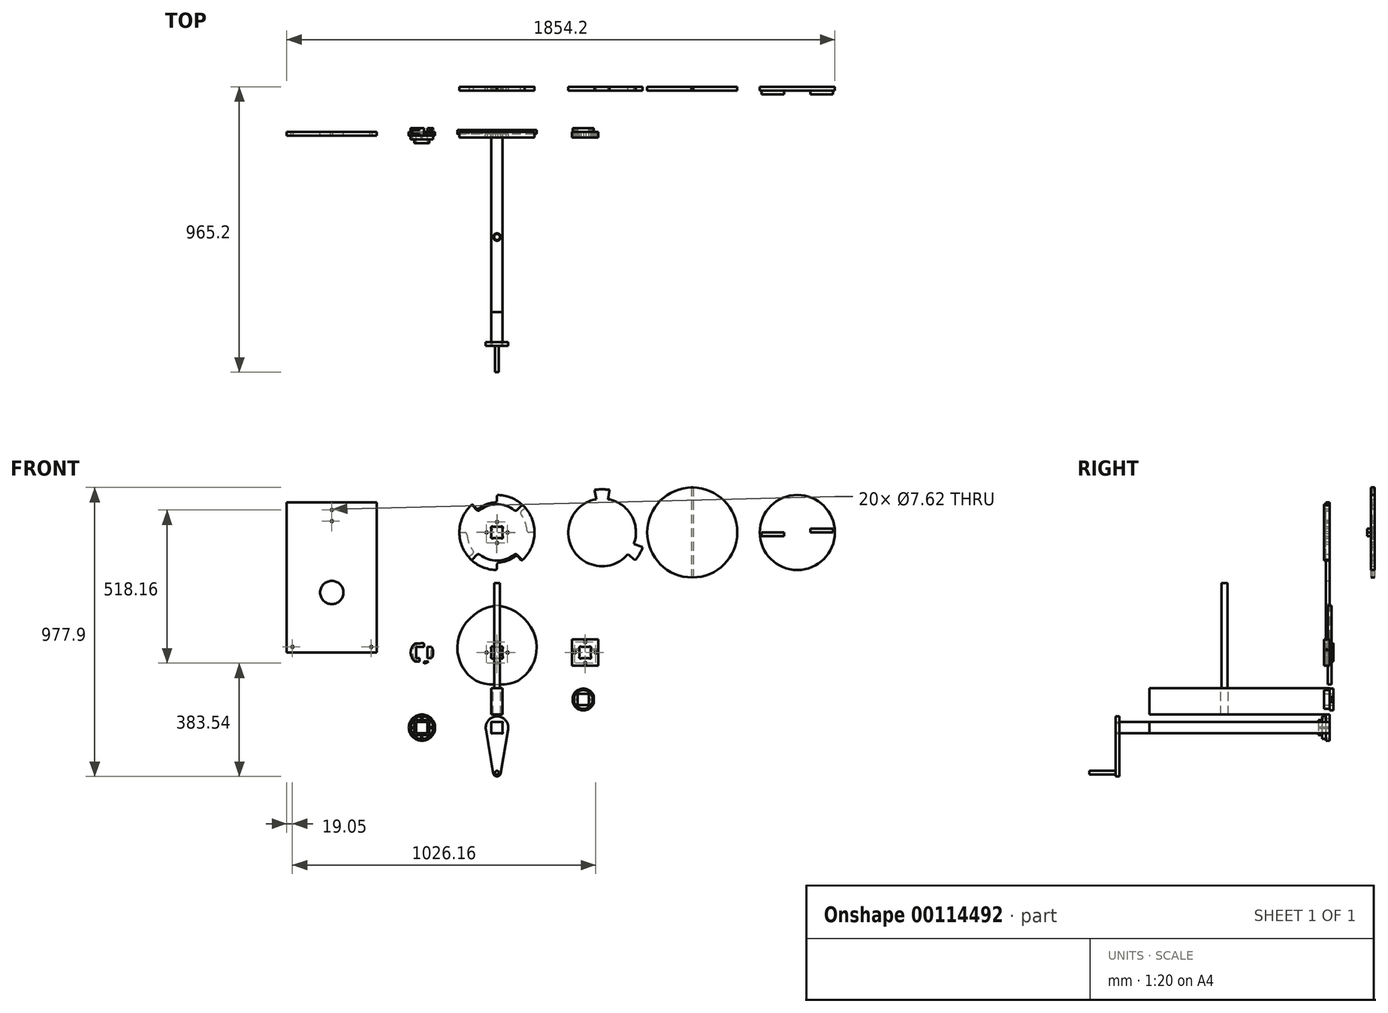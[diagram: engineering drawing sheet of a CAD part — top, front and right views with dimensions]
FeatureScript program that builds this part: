
annotation { "Feature Type Name" : "Feature", "Feature Type Description" : "" }
export const myFeature = defineFeature(function(context is Context, id is Id, definition is map)
    precondition{}
    {
        {
            var Q0;
            Q0=qCreatedBy(makeId("Front.planeOp"),FACE);
            var sketch = newSketch(context, id + "F0", { "sketchPlane" : qUnion([Q0])});
            skLineSegment(sketch, "E0", {"start": v(-177.8, 0) * mm, "end": v(177.8, 0) * mm, "construction": true});
            skLineSegment(sketch, "E1", {"start": v(0, 177.8) * mm, "end": v(0, -177.8) * mm, "construction": true});
            skLineSegment(sketch, "E2.bottom", {"start": v(-12.7, -19.05) * mm, "end": v(12.7, -19.05) * mm});
            skLineSegment(sketch, "E2.top", {"start": v(-12.7, 19.05) * mm, "end": v(12.7, 19.05) * mm});
            skLineSegment(sketch, "E2.left", {"start": v(-19.05, -12.7) * mm, "end": v(-19.05, 12.7) * mm});
            skLineSegment(sketch, "E2.right", {"start": v(19.05, -12.7) * mm, "end": v(19.05, 12.7) * mm});
            skCircle(sketch, "E3", {"center": v(0, 0) * mm, "radius": 107.95 * mm, "construction": true});
            skCircle(sketch, "E4", {"center": v(0, 0) * mm, "radius": 158.75 * mm, "construction": true});
            skLineSegment(sketch, "E5", {"start": v(0, 0) * mm, "end": v(92.23, -159.75) * mm, "construction": true});
            skLineSegment(sketch, "E6", {"start": v(0, 0) * mm, "end": v(167.52, -96.72) * mm, "construction": true});
            skLineSegment(sketch, "E7", {"start": v(0, 0) * mm, "end": v(165.07, 95.3) * mm, "construction": true});
            skLineSegment(sketch, "E8", {"start": v(0, 0) * mm, "end": v(94.16, 163.09) * mm, "construction": true});
            skLineSegment(sketch, "E9", {"start": v(0, 0) * mm, "end": v(-88.3, 152.95) * mm, "construction": true});
            skLineSegment(sketch, "E10", {"start": v(0, 0) * mm, "end": v(-155.29, 89.66) * mm, "construction": true});
            skLineSegment(sketch, "E11", {"start": v(0, 0) * mm, "end": v(-153.33, -88.52) * mm, "construction": true});
            skLineSegment(sketch, "E12", {"start": v(0, 0) * mm, "end": v(-90.3, -156.42) * mm, "construction": true});
            skPoint(sketch, "E13", {"position": v(0, -107.95) * mm});
            skPoint(sketch, "E14", {"position": v(58.17, -100.75) * mm});
            skPoint(sketch, "E15", {"position": v(108, -62.36) * mm});
            skPoint(sketch, "E16", {"position": v(133.1, 0) * mm});
            skPoint(sketch, "E17", {"position": v(122.52, 70.74) * mm});
            skPoint(sketch, "E18", {"position": v(74.93, 129.78) * mm});
            skPoint(sketch, "E19", {"position": v(0, 158.75) * mm});
            skPoint(sketch, "E20.MirrorP", {"position": v(-74.93, 129.78) * mm});
            skPoint(sketch, "E21.MirrorP", {"position": v(-133.1, 0) * mm});
            skPoint(sketch, "E22.MirrorP", {"position": v(-108, -62.36) * mm});
            skPoint(sketch, "E23.MirrorP", {"position": v(-58.17, -100.75) * mm});
            skPoint(sketch, "E24.MirrorP", {"position": v(-122.52, 70.74) * mm});
            skFitSpline(sketch, "E25", {"points": [v(0, 158.75) * mm, v(-74.93, 129.78) * mm, v(-122.52, 70.74) * mm, v(-133.1, 0) * mm, v(-108, -62.36) * mm, v(-58.17, -100.75) * mm, v(0, -107.95) * mm, v(58.17, -100.75) * mm, v(108, -62.36) * mm, v(133.1, 0) * mm, v(122.52, 70.74) * mm, v(74.93, 129.78) * mm, v(0, 158.75) * mm]});
            skPoint(sketch, "E26.visualSharp", {"position": v(-19.05, 19.05) * mm});
            skPoint(sketch, "E27.visualSharp", {"position": v(19.05, 19.05) * mm});
            skPoint(sketch, "E28.visualSharp", {"position": v(19.05, -19.05) * mm});
            skPoint(sketch, "E29.visualSharp", {"position": v(-19.05, -19.05) * mm});
            skArc(sketch, "E30", {"start": v(-12.7, 19.05) * mm, "mid": v(-19.05, 19.05) * mm, "end": v(-19.05, 12.7) * mm});
            skLineSegment(sketch, "E31", {"start": v(-19.05, 12.7) * mm, "end": v(-19.05, 19.05) * mm, "construction": true});
            skLineSegment(sketch, "E32", {"start": v(-12.7, 19.05) * mm, "end": v(-19.05, 19.05) * mm, "construction": true});
            skLineSegment(sketch, "E33", {"start": v(-19.05, -12.7) * mm, "end": v(-19.05, -19.05) * mm, "construction": true});
            skLineSegment(sketch, "E34", {"start": v(-12.7, -19.05) * mm, "end": v(-19.05, -19.05) * mm, "construction": true});
            skArc(sketch, "E35", {"start": v(-19.05, -12.7) * mm, "mid": v(-19.05, -19.05) * mm, "end": v(-12.7, -19.05) * mm});
            skArc(sketch, "E36.MirrorC", {"start": v(12.7, 19.05) * mm, "mid": v(19.05, 19.05) * mm, "end": v(19.05, 12.7) * mm});
            skArc(sketch, "E37.MirrorC", {"start": v(19.05, -12.7) * mm, "mid": v(19.05, -19.05) * mm, "end": v(12.7, -19.05) * mm});
            skCircle(sketch, "E38", {"center": v(0, 35.56) * mm, "radius": 3.81 * mm});
            skCircle(sketch, "E39.MirrorC", {"center": v(0, -35.56) * mm, "radius": 3.81 * mm});
            skCircle(sketch, "E40", {"center": v(-35.56, 0) * mm, "radius": 3.81 * mm});
            skCircle(sketch, "E41.MirrorC", {"center": v(35.56, 0) * mm, "radius": 3.81 * mm});
            skSolve(sketch);
        }
        {
            var Q0;
            Q0=makeQuery(id+"F0.imprint","IMPRINT",FACE,{"disambiguationData":[TD([[makeQuery(id+"F0.imprint","IMPRINT",EDGE,{"derivedFrom":sQuery(id+"F0.wireOp",EDGE,"E2.bottom")}),-1.0]])]});
            extrude(context, id + "F1", {"entities" : qUnion([Q0]), "endBound" : BoundingType.SYMMETRIC, "depth" : 12.7 * mm});
        }
        {
            var Q0;
            Q0=qCreatedBy(makeId("Right.planeOp"),FACE);
            cPlane(context, id + "F2", {"entities" : qUnion([Q0]), "cplaneType" : CPlaneType.OFFSET, "offset" : 254 * mm, "oppositeDirection" : true, "width" : 152.4 * mm, "height" : 152.4 * mm});
        }
        {
            var Q0;
            Q0=qCreatedBy(makeId("Front.planeOp"),FACE);
            var sketch = newSketch(context, id + "F3", { "sketchPlane" : qUnion([Q0])});
            skPoint(sketch, "E42", {"position": v(-254, 0) * mm});
            skCircle(sketch, "E43", {"center": v(-254, 0) * mm, "radius": 38.1 * mm});
            skCircle(sketch, "E44", {"center": v(-254, 0) * mm, "radius": 31.75 * mm});
            skLineSegment(sketch, "E45", {"start": v(-254, -101.35) * mm, "end": v(-254, 100.54) * mm, "construction": true});
            skLineSegment(sketch, "E46", {"start": v(-330.2, 0) * mm, "end": v(-154.12, 0) * mm, "construction": true});
            skLineSegment(sketch, "E47.bottom", {"start": v(-273.05, -19.05) * mm, "end": v(-234.95, -19.05) * mm});
            skLineSegment(sketch, "E47.top", {"start": v(-273.05, 19.05) * mm, "end": v(-234.95, 19.05) * mm});
            skLineSegment(sketch, "E47.left", {"start": v(-273.05, -19.05) * mm, "end": v(-273.05, 19.05) * mm});
            skLineSegment(sketch, "E47.right", {"start": v(-234.95, -19.05) * mm, "end": v(-234.95, 19.05) * mm});
            skLineSegment(sketch, "E48", {"start": v(-246.38, 37.33) * mm, "end": v(-246.38, -37.33) * mm});
            skLineSegment(sketch, "E49.MirrorCS", {"start": v(-261.62, 37.33) * mm, "end": v(-261.62, -37.33) * mm});
            skLineSegment(sketch, "E50", {"start": v(-231.6, 30.82) * mm, "end": v(-276.4, 30.82) * mm});
            skLineSegment(sketch, "E51.MirrorCS", {"start": v(-231.6, -30.82) * mm, "end": v(-276.4, -30.82) * mm});
            skPoint(sketch, "E52", {"position": v(-261.62, 30.82) * mm});
            skLineSegment(sketch, "E53", {"start": v(-234.95, 19.05) * mm, "end": v(-221, 19.05) * mm});
            skLineSegment(sketch, "E54", {"start": v(-234.95, -19.05) * mm, "end": v(-221, -19.05) * mm});
            skSolve(sketch);
        }
        {
            var Q0;
            {var subQ0=sQuery(id+"F3.wireOp",EDGE,"E47.left");Q0=makeQuery(id+"F3.imprint","IMPRINT",FACE,{"disambiguationData":[TD([[makeQuery(id+"F3.imprint","IMPRINT",EDGE,{"derivedFrom":subQ0}),1.0]])]});}
            extrude(context, id + "F4", {"entities" : qUnion([Q0]), "depth" : 6.35 * mm});
        }
        {
            var Q0;
            {var subQ6=sQuery(id+"F3.wireOp",EDGE,"E50");var subQ8=sQuery(id+"F3.wireOp",EDGE,"E43");var subQ9=makeQuery(id+"F3.imprint","INTERSECT",VERTEX,{"disambiguationData":[OD(1.0)],"derivedFrom":[subQ8,subQ6]});Q0=makeQuery(id+"F3.imprint","IMPRINT",FACE,{"disambiguationData":[TD([[makeQuery(id+"F3.imprint","IMPRINT",EDGE,{"disambiguationData":[TD([[subQ9,-1.0]])],"derivedFrom":subQ8}),1.0]])]});}
            var Q1;
            {var subQ0=sQuery(id+"F3.wireOp",EDGE,"E47.left");Q1=makeQuery(id+"F3.imprint","IMPRINT",FACE,{"disambiguationData":[TD([[makeQuery(id+"F3.imprint","IMPRINT",EDGE,{"derivedFrom":subQ0}),1.0]])]});}
            extrude(context, id + "F5", {"entities" : qUnion([Q0, Q1]), "operationType" : NewBodyOperationType.ADD, "depth" : 12.7 * mm, "hasSecondDirection" : true, "secondDirectionOppositeDirection" : false, "secondDirectionDepth" : 6.35 * mm});
        }
        {
            var Q0;
            Q0=makeQuery(id+"F4.opExtrude","SWEPT_BODY",BODY,{"disambiguationData":[OSD([sQuery(id+"F3.wireOp",EDGE,"E44"),sQuery(id+"F3.wireOp",EDGE,"E47.bottom"),sQuery(id+"F3.wireOp",EDGE,"E47.top"),sQuery(id+"F3.wireOp",EDGE,"E47.left"),sQuery(id+"F3.wireOp",EDGE,"E49.MirrorCS")])]});
            var Q1;
            Q1=qCreatedBy(makeId("Front.planeOp"),FACE);
            mirror(context, id + "F6", {"operationType" : NewBodyOperationType.ADD, "entities" : qUnion([Q0]), "mirrorPlane" : qUnion([Q1])});
        }
        {
            var Q0;
            Q0=qCreatedBy(makeId("Front.planeOp"),FACE);
            var sketch = newSketch(context, id + "F7", { "sketchPlane" : qUnion([Q0])});
            skLineSegment(sketch, "E55.bottom", {"start": v(-406.4, 0) * mm, "end": v(-711.2, 0) * mm});
            skLineSegment(sketch, "E55.top", {"start": v(-406.4, 508) * mm, "end": v(-711.2, 508) * mm});
            skLineSegment(sketch, "E55.left", {"start": v(-406.4, 0) * mm, "end": v(-406.4, 508) * mm});
            skLineSegment(sketch, "E55.right", {"start": v(-711.2, 0) * mm, "end": v(-711.2, 508) * mm});
            skLineSegment(sketch, "E56", {"start": v(-558.8, 508) * mm, "end": v(-558.8, 0) * mm, "construction": true});
            skLineSegment(sketch, "E57", {"start": v(-711.2, 254) * mm, "end": v(-406.4, 254) * mm, "construction": true});
            skCircle(sketch, "E58", {"center": v(-558.8, 203.2) * mm, "radius": 39.37 * mm});
            skLineSegment(sketch, "E59.bottom", {"start": v(-577.85, 508) * mm, "end": v(-539.75, 508) * mm, "construction": true});
            skLineSegment(sketch, "E59.top", {"start": v(-577.85, 419.1) * mm, "end": v(-539.75, 419.1) * mm, "construction": true});
            skLineSegment(sketch, "E59.left", {"start": v(-577.85, 508) * mm, "end": v(-577.85, 419.1) * mm, "construction": true});
            skLineSegment(sketch, "E59.right", {"start": v(-539.75, 508) * mm, "end": v(-539.75, 419.1) * mm, "construction": true});
            skCircle(sketch, "E60", {"center": v(-558.8, 482.6) * mm, "radius": 3.81 * mm});
            skCircle(sketch, "E61", {"center": v(-558.8, 444.5) * mm, "radius": 3.81 * mm});
            skCircle(sketch, "E62", {"center": v(-692.15, 19.05) * mm, "radius": 3.81 * mm});
            skCircle(sketch, "E63.MirrorC", {"center": v(-425.45, 19.05) * mm, "radius": 3.81 * mm});
            skSolve(sketch);
        }
        {
            var Q0;
            Q0=makeQuery(id+"F7.imprint","IMPRINT",FACE,{"disambiguationData":[TD([[makeQuery(id+"F7.imprint","IMPRINT",EDGE,{"derivedFrom":sQuery(id+"F7.wireOp",EDGE,"E55.bottom")}),-1.0]])]});
            extrude(context, id + "F8", {"entities" : qUnion([Q0]), "depth" : 12.7 * mm});
        }
        {
            var Q0;
            {var subQ0=sQuery(id+"F3.wireOp",EDGE,"E49.MirrorCS");var subQ1=sQuery(id+"F3.wireOp",EDGE,"E47.top");var subQ2=makeQuery(id+"F3.imprint","INTERSECT",VERTEX,{"derivedFrom":[subQ1,subQ0]});Q0=makeQuery(id+"F3.imprint","IMPRINT",FACE,{"disambiguationData":[TD([[makeQuery(id+"F3.imprint","IMPRINT",EDGE,{"disambiguationData":[TD([[subQ2,-1.0]])],"derivedFrom":subQ1}),1.0]])]});}
            var Q1;
            {var subQ0=sQuery(id+"F3.wireOp",EDGE,"E50");var subQ1=sQuery(id+"F3.wireOp",EDGE,"E44");var subQ2=makeQuery(id+"F3.imprint","INTERSECT",VERTEX,{"derivedFrom":[subQ1,sQuery(id+"F3.wireOp",EDGE,"E49.MirrorCS"),subQ0]});Q1=makeQuery(id+"F3.imprint","IMPRINT",FACE,{"disambiguationData":[TD([[makeQuery(id+"F3.imprint","IMPRINT",EDGE,{"disambiguationData":[TD([[subQ2,1.0]])],"derivedFrom":subQ1}),1.0]])]});}
            extrude(context, id + "F9", {"entities" : qUnion([Q0, Q1]), "depth" : 12.7 * mm});
        }
        {
            var Q0;
            {var subQ0=sQuery(id+"F3.wireOp",EDGE,"E48");var subQ1=sQuery(id+"F3.wireOp",EDGE,"E43");var subQ2=makeQuery(id+"F3.imprint","INTERSECT",VERTEX,{"disambiguationData":[OD(0.0)],"derivedFrom":[subQ1,subQ0]});Q0=makeQuery(id+"F3.imprint","IMPRINT",FACE,{"disambiguationData":[TD([[makeQuery(id+"F3.imprint","IMPRINT",EDGE,{"disambiguationData":[TD([[subQ2,-1.0]])],"derivedFrom":subQ1}),1.0]])]});}
            var Q1;
            Q1=makeQuery(id+"F5.opExtrude","CAP_FACE",FACE,{"disambiguationData":[OSD([sQuery(id+"F3.wireOp",EDGE,"E43"),sQuery(id+"F3.wireOp",EDGE,"E47.bottom"),sQuery(id+"F3.wireOp",EDGE,"E47.top"),sQuery(id+"F3.wireOp",EDGE,"E47.left"),sQuery(id+"F3.wireOp",EDGE,"E49.MirrorCS"),sQuery(id+"F3.wireOp",EDGE,"E50"),sQuery(id+"F3.wireOp",EDGE,"E51.MirrorCS")])],"isStart":false});
            var Q2;
            Q2=makeQuery(id+"F5.opExtrude","CAP_FACE",FACE,{"disambiguationData":[OSD([sQuery(id+"F3.wireOp",EDGE,"E43"),sQuery(id+"F3.wireOp",EDGE,"E47.bottom"),sQuery(id+"F3.wireOp",EDGE,"E47.top"),sQuery(id+"F3.wireOp",EDGE,"E47.left"),sQuery(id+"F3.wireOp",EDGE,"E49.MirrorCS"),sQuery(id+"F3.wireOp",EDGE,"E50"),sQuery(id+"F3.wireOp",EDGE,"E51.MirrorCS")])],"isStart":true});
            extrude(context, id + "F10", {"entities" : qUnion([Q0]), "operationType" : NewBodyOperationType.ADD, "endBound" : BoundingType.UP_TO_SURFACE, "endBoundEntityFace" : qUnion([Q1]), "depth" : 50.42 * mm, "hasSecondDirection" : true, "secondDirectionBound" : SecondDirectionBoundingType.UP_TO_SURFACE, "secondDirectionOppositeDirection" : false, "secondDirectionBoundEntityFace" : qUnion([Q2]), "secondDirectionDepth" : 0.5 * mm});
        }
        {
            var Q0;
            Q0=makeQuery(id+"F9.opExtrude","SWEPT_BODY",BODY,{"disambiguationData":[OSD([sQuery(id+"F3.wireOp",EDGE,"E44"),sQuery(id+"F3.wireOp",EDGE,"E47.top"),sQuery(id+"F3.wireOp",EDGE,"E48"),sQuery(id+"F3.wireOp",EDGE,"E49.MirrorCS")])]});
            var Q1;
            Q1=qCreatedBy(makeId("Front.planeOp"),FACE);
            mirror(context, id + "F11", {"operationType" : NewBodyOperationType.ADD, "entities" : qUnion([Q0]), "mirrorPlane" : qUnion([Q1])});
        }
        {
            var Q0;
            {var subQ5=sQuery(id+"F3.wireOp",EDGE,"E47.right");Q0=makeQuery(id+"F3.imprint","IMPRINT",FACE,{"disambiguationData":[TD([[makeQuery(id+"F3.imprint","IMPRINT",EDGE,{"derivedFrom":subQ5}),-1.0]])]});}
            extrude(context, id + "F12", {"entities" : qUnion([Q0]), "depth" : 12.7 * mm});
        }
        {
            var Q0;
            {var subQ0=sQuery(id+"F3.wireOp",EDGE,"E53");var subQ1=sQuery(id+"F3.wireOp",EDGE,"E43");var subQ2=makeQuery(id+"F3.imprint","INTERSECT",VERTEX,{"derivedFrom":[subQ1,subQ0]});Q0=makeQuery(id+"F3.imprint","IMPRINT",FACE,{"disambiguationData":[TD([[makeQuery(id+"F3.imprint","IMPRINT",EDGE,{"disambiguationData":[TD([[subQ2,1.0]])],"derivedFrom":subQ1}),1.0]])]});}
            extrude(context, id + "F13", {"entities" : qUnion([Q0]), "operationType" : NewBodyOperationType.ADD, "depth" : 12.7 * mm, "hasSecondDirection" : true, "secondDirectionOppositeDirection" : false, "secondDirectionDepth" : 6.35 * mm});
        }
        {
            var Q0;
            Q0=makeQuery(id+"F12.opExtrude","SWEPT_BODY",BODY,{"disambiguationData":[OSD([sQuery(id+"F3.wireOp",EDGE,"E44"),sQuery(id+"F3.wireOp",EDGE,"E47.right"),sQuery(id+"F3.wireOp",EDGE,"E53"),sQuery(id+"F3.wireOp",EDGE,"E54")])]});
            var Q1;
            Q1=qCreatedBy(makeId("Front.planeOp"),FACE);
            mirror(context, id + "F14", {"operationType" : NewBodyOperationType.ADD, "entities" : qUnion([Q0]), "mirrorPlane" : qUnion([Q1])});
        }
        {
            var Q0;
            Q0=qCreatedBy(makeId("Top.planeOp"),FACE);
            cPlane(context, id + "F15", {"entities" : qUnion([Q0]), "cplaneType" : CPlaneType.OFFSET, "offset" : 254 * mm, "oppositeDirection" : true, "width" : 152.4 * mm, "height" : 152.4 * mm});
        }
        {
            var Q0;
            Q0=qCreatedBy(makeId("Front.planeOp"),FACE);
            var sketch = newSketch(context, id + "F16", { "sketchPlane" : qUnion([Q0])});
            skLineSegment(sketch, "E64", {"start": v(-254, -173.27) * mm, "end": v(-254, -360.68) * mm, "construction": true});
            skLineSegment(sketch, "E65", {"start": v(-334.3, -254) * mm, "end": v(-157.43, -254) * mm, "construction": true});
            skLineSegment(sketch, "E66.bottom", {"start": v(-273.05, -234.95) * mm, "end": v(-234.95, -234.95) * mm});
            skLineSegment(sketch, "E66.top", {"start": v(-273.05, -273.05) * mm, "end": v(-234.95, -273.05) * mm});
            skLineSegment(sketch, "E66.left", {"start": v(-273.05, -234.95) * mm, "end": v(-273.05, -273.05) * mm});
            skLineSegment(sketch, "E66.right", {"start": v(-234.95, -234.95) * mm, "end": v(-234.95, -273.05) * mm});
            skPoint(sketch, "E67", {"position": v(-254, -234.95) * mm});
            skPoint(sketch, "E68", {"position": v(-273.05, -254) * mm});
            skCircle(sketch, "E69", {"center": v(-254, -254) * mm, "radius": 38.1 * mm});
            skCircle(sketch, "E70", {"center": v(-254, -254) * mm, "radius": 44.45 * mm});
            skLineSegment(sketch, "E71.bottom", {"start": v(-279.4, -228.6) * mm, "end": v(-228.6, -228.6) * mm});
            skLineSegment(sketch, "E71.top", {"start": v(-279.4, -279.4) * mm, "end": v(-228.6, -279.4) * mm});
            skLineSegment(sketch, "E71.left", {"start": v(-279.4, -228.6) * mm, "end": v(-279.4, -279.4) * mm});
            skLineSegment(sketch, "E71.right", {"start": v(-228.6, -228.6) * mm, "end": v(-228.6, -279.4) * mm});
            skLineSegment(sketch, "E72", {"start": v(-273.05, -234.95) * mm, "end": v(-279.4, -234.95) * mm, "construction": true});
            skLineSegment(sketch, "E73", {"start": v(-273.05, -234.95) * mm, "end": v(-273.05, -228.6) * mm, "construction": true});
            skLineSegment(sketch, "E74", {"start": v(-234.95, -234.95) * mm, "end": v(-228.6, -234.95) * mm, "construction": true});
            skLineSegment(sketch, "E75", {"start": v(-273.05, -273.05) * mm, "end": v(-273.05, -279.4) * mm, "construction": true});
            skCircle(sketch, "E76", {"center": v(-254, -220.98) * mm, "radius": 2.54 * mm});
            skCircle(sketch, "E77", {"center": v(-254, -287.02) * mm, "radius": 2.54 * mm});
            skCircle(sketch, "E78", {"center": v(-287.02, -254) * mm, "radius": 2.54 * mm});
            skCircle(sketch, "E79.MirrorC", {"center": v(-220.98, -254) * mm, "radius": 2.54 * mm});
            skSolve(sketch);
        }
        {
            var Q0;
            Q0=makeQuery(id+"F16.imprint","IMPRINT",FACE,{"disambiguationData":[TD([[makeQuery(id+"F16.imprint","IMPRINT",EDGE,{"derivedFrom":sQuery(id+"F16.wireOp",EDGE,"E66.bottom")}),1.0]])]});
            extrude(context, id + "F17", {"entities" : qUnion([Q0]), "depth" : 38.1 * mm});
        }
        {
            var Q0;
            Q0=makeQuery(id+"F16.imprint","IMPRINT",FACE,{"disambiguationData":[TD([[makeQuery(id+"F16.imprint","IMPRINT",EDGE,{"derivedFrom":sQuery(id+"F16.wireOp",EDGE,"E69")}),1.0]])]});
            extrude(context, id + "F18", {"entities" : qUnion([Q0]), "operationType" : NewBodyOperationType.ADD, "depth" : 25.4 * mm});
        }
        {
            var Q0;
            Q0=makeQuery(id+"F16.imprint","IMPRINT",FACE,{"disambiguationData":[TD([[makeQuery(id+"F16.imprint","IMPRINT",EDGE,{"derivedFrom":sQuery(id+"F16.wireOp",EDGE,"E69")}),-1.0]])]});
            extrude(context, id + "F19", {"entities" : qUnion([Q0]), "operationType" : NewBodyOperationType.ADD, "depth" : 12.7 * mm});
        }
        {
            var Q0;
            Q0=makeQuery(id+"F17.opExtrude","SWEPT_FACE",FACE,{"disambiguationData":[OSD([sQuery(id+"F16.wireOp",EDGE,"E71.left")])]});
            var sketch = newSketch(context, id + "F20", { "sketchPlane" : qUnion([Q0])});
            skLineSegment(sketch, "E80.0", {"start": v(25.4, -215.9) * mm, "end": v(25.4, -292.1) * mm, "construction": true});
            skLineSegment(sketch, "E81.0", {"start": v(38.1, -228.6) * mm, "end": v(38.1, -279.4) * mm, "construction": true});
            skLineSegment(sketch, "E82", {"start": v(25.4, -254) * mm, "end": v(38.1, -254) * mm, "construction": true});
            skCircle(sketch, "E83", {"center": v(31.75, -254) * mm, "radius": 2.54 * mm});
            skSolve(sketch);
        }
        {
            var Q0;
            Q0=makeQuery(id+"F20.imprint","IMPRINT",FACE,{"disambiguationData":[TD([[makeQuery(id+"F20.imprint","IMPRINT",EDGE,{"derivedFrom":sQuery(id+"F20.wireOp",EDGE,"E83")}),1.0]])]});
            extrude(context, id + "F21", {"entities" : qUnion([Q0]), "operationType" : NewBodyOperationType.REMOVE, "endBound" : BoundingType.THROUGH_ALL, "oppositeDirection" : true, "depth" : 25.4 * mm});
        }
        {
            var Q0;
            Q0=qCreatedBy(makeId("Front.planeOp"),FACE);
            var sketch = newSketch(context, id + "F22", { "sketchPlane" : qUnion([Q0])});
            skLineSegment(sketch, "E84.bottom", {"start": v(-19.05, -273.05) * mm, "end": v(19.05, -273.05) * mm});
            skLineSegment(sketch, "E84.top", {"start": v(-19.05, -234.95) * mm, "end": v(19.05, -234.95) * mm});
            skLineSegment(sketch, "E84.left", {"start": v(-19.05, -234.95) * mm, "end": v(-19.05, -273.05) * mm});
            skLineSegment(sketch, "E84.right", {"start": v(19.05, -234.95) * mm, "end": v(19.05, -273.05) * mm});
            skPoint(sketch, "E85", {"position": v(0, -273.05) * mm});
            skPoint(sketch, "E86", {"position": v(19.05, -254) * mm});
            skSolve(sketch);
        }
        {
            var Q0;
            Q0=makeQuery(id+"F22.imprint","IMPRINT",FACE,{"disambiguationData":[TD([[makeQuery(id+"F22.imprint","IMPRINT",EDGE,{"derivedFrom":sQuery(id+"F22.wireOp",EDGE,"E84.bottom")}),1.0]])]});
            extrude(context, id + "F23", {"entities" : qUnion([Q0]), "depth" : 711.2 * mm});
        }
        {
            var Q0;
            Q0 = qSketchRegion(id + "F22", true);
            extrude(context, id + "F24", {"entities" : qUnion([Q0]), "depth" : 609.6 * mm});
        }
        {
            var Q0;
            Q0=qCreatedBy(makeId("Front.planeOp"),FACE);
            var sketch = newSketch(context, id + "F25", { "sketchPlane" : qUnion([Q0])});
            skLineSegment(sketch, "E87", {"start": v(0, 0) * mm, "end": v(0, -304.67) * mm, "construction": true});
            skLineSegment(sketch, "E88.bottom", {"start": v(-19.05, -120.65) * mm, "end": v(19.05, -120.65) * mm});
            skLineSegment(sketch, "E88.top", {"start": v(-19.05, -209.55) * mm, "end": v(19.05, -209.55) * mm});
            skLineSegment(sketch, "E88.left", {"start": v(-19.05, -120.65) * mm, "end": v(-19.05, -209.55) * mm});
            skLineSegment(sketch, "E88.right", {"start": v(19.05, -120.65) * mm, "end": v(19.05, -209.55) * mm});
            skSolve(sketch);
        }
        {
            var Q0;
            Q0=makeQuery(id+"F25.imprint","IMPRINT",FACE,{"disambiguationData":[TD([[makeQuery(id+"F25.imprint","IMPRINT",EDGE,{"derivedFrom":sQuery(id+"F25.wireOp",EDGE,"E88.bottom")}),-1.0]])]});
            extrude(context, id + "F26", {"entities" : qUnion([Q0]), "depth" : 609.6 * mm});
        }
        {
            var Q0;
            Q0=makeQuery(id+"F26.opExtrude","SWEPT_FACE",FACE,{"disambiguationData":[OSD([sQuery(id+"F25.wireOp",EDGE,"E88.bottom")])]});
            var sketch = newSketch(context, id + "F27", { "sketchPlane" : qUnion([Q0])});
            skLineSegment(sketch, "E89", {"start": v(0, 0) * mm, "end": v(0, -621.23) * mm, "construction": true});
            skPoint(sketch, "E89.endSnap0", {"position": v(0, -609.6) * mm});
            skCircle(sketch, "E90", {"center": v(0, -355.6) * mm, "radius": 12.7 * mm});
            skSolve(sketch);
        }
        {
            var Q0;
            Q0=makeQuery(id+"F27.imprint","IMPRINT",FACE,{"disambiguationData":[TD([[makeQuery(id+"F27.imprint","IMPRINT",EDGE,{"derivedFrom":sQuery(id+"F27.wireOp",EDGE,"E90")}),1.0]])]});
            var Q1;
            Q1=makeQuery(id+"F26.opExtrude","SWEPT_FACE",FACE,{"disambiguationData":[OSD([sQuery(id+"F25.wireOp",EDGE,"E88.top")])]});
            extrude(context, id + "F28", {"entities" : qUnion([Q0]), "operationType" : NewBodyOperationType.REMOVE, "endBound" : BoundingType.UP_TO_SURFACE, "oppositeDirection" : true, "endBoundEntityFace" : qUnion([Q1]), "depth" : 25.4 * mm});
        }
        {
            var Q0;
            Q0=makeQuery(id+"F26.opExtrude","SWEPT_FACE",FACE,{"disambiguationData":[OSD([sQuery(id+"F25.wireOp",EDGE,"E88.bottom")])]});
            var sketch = newSketch(context, id + "F29", { "sketchPlane" : qUnion([Q0])});
            skCircle(sketch, "E91.0", {"center": v(0, -355.6) * mm, "radius": 9.9 * mm});
            skSolve(sketch);
        }
        {
            var Q0;
            Q0=makeQuery(id+"F29.imprint","IMPRINT",FACE,{"disambiguationData":[TD([[makeQuery(id+"F29.imprint","IMPRINT",EDGE,{"derivedFrom":sQuery(id+"F29.wireOp",EDGE,"E91.0")}),1.0]])]});
            extrude(context, id + "F30", {"entities" : qUnion([Q0]), "depth" : 355.6 * mm});
        }
        {
            var Q0;
            Q0=makeQuery(id+"F23.opExtrude","CAP_FACE",FACE,{"disambiguationData":[OSD([sQuery(id+"F22.wireOp",EDGE,"E84.bottom"),sQuery(id+"F22.wireOp",EDGE,"E84.top"),sQuery(id+"F22.wireOp",EDGE,"E84.left"),sQuery(id+"F22.wireOp",EDGE,"E84.right")])],"isStart":false});
            var sketch = newSketch(context, id + "F31", { "sketchPlane" : qUnion([Q0])});
            skCircle(sketch, "E92", {"center": v(0, -254) * mm, "radius": 38.1 * mm});
            skPoint(sketch, "E92.centerSnap0", {"position": v(19.05, -254) * mm});
            skPoint(sketch, "E92.centerSnap1", {"position": v(0, -234.95) * mm});
            skCircle(sketch, "E93", {"center": v(0, -406.4) * mm, "radius": 12.7 * mm});
            skPoint(sketch, "E93.centerSnap0", {"position": v(0, -273.05) * mm});
            skLineSegment(sketch, "E94", {"start": v(-37.57, -260.35) * mm, "end": v(-12.52, -408.52) * mm});
            skLineSegment(sketch, "E95", {"start": v(37.57, -260.35) * mm, "end": v(12.52, -408.52) * mm});
            skCircle(sketch, "E96", {"center": v(0, -406.4) * mm, "radius": 6.35 * mm});
            skArc(sketch, "E97", {"start": v(-15.87, -234.95) * mm, "mid": v(-19.05, -234.95) * mm, "end": v(-19.05, -238.12) * mm});
            skLineSegment(sketch, "E98", {"start": v(0, -254) * mm, "end": v(-19.05, -234.95) * mm, "construction": true});
            skLineSegment(sketch, "E99", {"start": v(0, -234.95) * mm, "end": v(0, -273.05) * mm, "construction": true});
            skLineSegment(sketch, "E100", {"start": v(19.05, -254) * mm, "end": v(-19.05, -254) * mm, "construction": true});
            skArc(sketch, "E101.MirrorC", {"start": v(15.87, -234.95) * mm, "mid": v(19.05, -234.95) * mm, "end": v(19.05, -238.12) * mm});
            skLineSegment(sketch, "E102", {"start": v(-15.87, -234.95) * mm, "end": v(15.87, -234.95) * mm});
            skLineSegment(sketch, "E103.MirrorC", {"start": v(15.87, -269.88) * mm, "end": v(15.87, -269.88) * mm});
            skArc(sketch, "E104.MirrorC", {"start": v(-15.87, -273.05) * mm, "mid": v(-19.05, -273.05) * mm, "end": v(-19.05, -269.88) * mm});
            skLineSegment(sketch, "E105.MirrorCS", {"start": v(0, -254) * mm, "end": v(-19.05, -273.05) * mm, "construction": true});
            skLineSegment(sketch, "E106.MirrorCS", {"start": v(0, -254) * mm, "end": v(19.05, -234.95) * mm, "construction": true});
            skLineSegment(sketch, "E107.MirrorCS", {"start": v(0, -254) * mm, "end": v(19.05, -273.05) * mm, "construction": true});
            skLineSegment(sketch, "E108", {"start": v(-19.05, -238.12) * mm, "end": v(-19.05, -269.88) * mm});
            skLineSegment(sketch, "E109", {"start": v(-15.87, -273.05) * mm, "end": v(15.87, -273.05) * mm});
            skLineSegment(sketch, "E110", {"start": v(19.05, -269.88) * mm, "end": v(19.05, -238.12) * mm});
            skArc(sketch, "E111.trimOffspring", {"start": v(15.87, -273.05) * mm, "mid": v(19.05, -273.05) * mm, "end": v(19.05, -269.88) * mm});
            skSolve(sketch);
        }
        {
            var Q0;
            {var subQ0=sQuery(id+"F31.wireOp",EDGE,"E94");Q0=makeQuery(id+"F31.imprint","IMPRINT",FACE,{"disambiguationData":[TD([[makeQuery(id+"F31.imprint","IMPRINT",EDGE,{"derivedFrom":subQ0}),1.0]])]});}
            var Q1;
            Q1=makeQuery(id+"F31.imprint","IMPRINT",FACE,{"disambiguationData":[TD([[makeQuery(id+"F31.imprint","IMPRINT",EDGE,{"derivedFrom":sQuery(id+"F31.wireOp",EDGE,"E96")}),-1.0]])]});
            var Q2;
            {var subQ13=sQuery(id+"F31.wireOp",EDGE,"E102");Q2=makeQuery(id+"F31.imprint","IMPRINT",FACE,{"disambiguationData":[TD([[makeQuery(id+"F31.imprint","IMPRINT",EDGE,{"derivedFrom":subQ13}),1.0]])]});}
            extrude(context, id + "F32", {"entities" : qUnion([Q0, Q1, Q2]), "depth" : 12.7 * mm});
        }
        {
            var Q0;
            Q0=makeQuery(id+"F31.imprint","IMPRINT",FACE,{"disambiguationData":[TD([[makeQuery(id+"F31.imprint","IMPRINT",EDGE,{"derivedFrom":sQuery(id+"F31.wireOp",EDGE,"E96")}),1.0]])]});
            extrude(context, id + "F33", {"entities" : qUnion([Q0]), "operationType" : NewBodyOperationType.ADD, "depth" : 101.6 * mm});
        }
        {
            var Q0;
            Q0=qCreatedBy(makeId("Front.planeOp"),FACE);
            var sketch = newSketch(context, id + "F34", { "sketchPlane" : qUnion([Q0])});
            skLineSegment(sketch, "E112", {"start": v(0, 0) * mm, "end": v(468.82, 0) * mm, "construction": true});
            skLineSegment(sketch, "E113", {"start": v(298.45, 119.79) * mm, "end": v(298.45, -116.25) * mm, "construction": true});
            skLineSegment(sketch, "E114.bottom", {"start": v(254, 44.45) * mm, "end": v(342.9, 44.45) * mm});
            skLineSegment(sketch, "E114.top", {"start": v(254, -44.45) * mm, "end": v(342.9, -44.45) * mm});
            skLineSegment(sketch, "E114.left", {"start": v(254, 44.45) * mm, "end": v(254, -44.45) * mm});
            skLineSegment(sketch, "E114.right", {"start": v(342.9, 44.45) * mm, "end": v(342.9, -44.45) * mm});
            skLineSegment(sketch, "E115.bottom", {"start": v(279.4, 19.05) * mm, "end": v(317.5, 19.05) * mm});
            skLineSegment(sketch, "E115.top", {"start": v(279.4, -19.05) * mm, "end": v(317.5, -19.05) * mm});
            skLineSegment(sketch, "E115.left", {"start": v(279.4, 19.05) * mm, "end": v(279.4, -19.05) * mm});
            skLineSegment(sketch, "E115.right", {"start": v(317.5, 19.05) * mm, "end": v(317.5, -19.05) * mm});
            skLineSegment(sketch, "E116", {"start": v(279.4, 19.05) * mm, "end": v(298.45, 0) * mm, "construction": true});
            skCircle(sketch, "E117", {"center": v(282.58, 15.87) * mm, "radius": 4.5 * mm});
            skPoint(sketch, "E117.first.point", {"position": v(285.75, 19.05) * mm});
            skPoint(sketch, "E117.second.point", {"position": v(279.4, 12.7) * mm});
            skCircle(sketch, "E118.MirrorC", {"center": v(314.32, 15.87) * mm, "radius": 4.5 * mm});
            skCircle(sketch, "E119.MirrorC", {"center": v(282.58, -15.87) * mm, "radius": 4.5 * mm});
            skCircle(sketch, "E120.MirrorC", {"center": v(314.32, -15.87) * mm, "radius": 4.5 * mm});
            skCircle(sketch, "E121", {"center": v(262.9, 0) * mm, "radius": 3.81 * mm});
            skCircle(sketch, "E122.MirrorC", {"center": v(334, 0) * mm, "radius": 3.81 * mm});
            skCircle(sketch, "E123.MirrorC", {"center": v(298.45, 35.56) * mm, "radius": 3.81 * mm});
            skCircle(sketch, "E124.MirrorC", {"center": v(298.45, -35.56) * mm, "radius": 3.81 * mm});
            skSolve(sketch);
        }
        {
            var Q0;
            Q0=makeQuery(id+"F34.imprint","IMPRINT",FACE,{"disambiguationData":[TD([[makeQuery(id+"F34.imprint","IMPRINT",EDGE,{"derivedFrom":sQuery(id+"F34.wireOp",EDGE,"E114.bottom")}),-1.0]])]});
            extrude(context, id + "F35", {"entities" : qUnion([Q0]), "depth" : 19.05 * mm});
        }
        {
            var Q0;
            Q0=makeQuery(id+"F35.opExtrude","SWEPT_FACE",FACE,{"disambiguationData":[OSD([sQuery(id+"F34.wireOp",EDGE,"E114.left")])]});
            var sketch = newSketch(context, id + "F36", { "sketchPlane" : qUnion([Q0])});
            skLineSegment(sketch, "E125", {"start": v(9.53, 44.45) * mm, "end": v(9.53, -44.45) * mm, "construction": true});
            skCircle(sketch, "E126", {"center": v(9.53, 9.52) * mm, "radius": 2.54 * mm});
            skSolve(sketch);
        }
        {
            var Q0;
            Q0=makeQuery(id+"F36.imprint","IMPRINT",FACE,{"disambiguationData":[TD([[makeQuery(id+"F36.imprint","IMPRINT",EDGE,{"derivedFrom":sQuery(id+"F36.wireOp",EDGE,"E126")}),1.0]])]});
            extrude(context, id + "F37", {"entities" : qUnion([Q0]), "operationType" : NewBodyOperationType.REMOVE, "endBound" : BoundingType.THROUGH_ALL, "oppositeDirection" : true, "depth" : 25.4 * mm});
        }
        {
            var Q0;
            Q0=qCreatedBy(makeId("Front.planeOp"),FACE);
            var sketch = newSketch(context, id + "F38", { "sketchPlane" : qUnion([Q0])});
            skCircle(sketch, "E127", {"center": v(292.1, -158.75) * mm, "radius": 31.75 * mm});
            skLineSegment(sketch, "E128", {"start": v(292.1, -190.5) * mm, "end": v(292.1, -127) * mm, "construction": true});
            skLineSegment(sketch, "E129", {"start": v(260.35, -158.75) * mm, "end": v(323.85, -158.75) * mm, "construction": true});
            skLineSegment(sketch, "E130.bottom", {"start": v(273.05, -139.7) * mm, "end": v(311.15, -139.7) * mm});
            skLineSegment(sketch, "E130.top", {"start": v(273.05, -177.8) * mm, "end": v(311.15, -177.8) * mm});
            skLineSegment(sketch, "E130.left", {"start": v(273.05, -139.7) * mm, "end": v(273.05, -177.8) * mm});
            skLineSegment(sketch, "E130.right", {"start": v(311.15, -139.7) * mm, "end": v(311.15, -177.8) * mm});
            skCircle(sketch, "E131", {"center": v(292.1, -158.75) * mm, "radius": 36.83 * mm});
            skLineSegment(sketch, "E132", {"start": v(327.84, -149.86) * mm, "end": v(327.84, -167.64) * mm});
            skLineSegment(sketch, "E133.MirrorCS", {"start": v(256.36, -149.86) * mm, "end": v(256.36, -167.64) * mm});
            skSolve(sketch);
        }
        {
            var Q0;
            Q0=makeQuery(id+"F38.imprint","IMPRINT",FACE,{"disambiguationData":[TD([[makeQuery(id+"F38.imprint","IMPRINT",EDGE,{"derivedFrom":sQuery(id+"F38.wireOp",EDGE,"E127")}),1.0]])]});
            extrude(context, id + "F39", {"entities" : qUnion([Q0]), "depth" : 19.05 * mm});
        }
        {
            var Q0;
            Q0=makeQuery(id+"F38.imprint","IMPRINT",FACE,{"disambiguationData":[TD([[makeQuery(id+"F38.imprint","IMPRINT",EDGE,{"derivedFrom":sQuery(id+"F38.wireOp",EDGE,"E127")}),-1.0]])]});
            var Q1;
            Q1=makeQuery(id+"F38.imprint","IMPRINT",FACE,{"disambiguationData":[TD([[makeQuery(id+"F38.imprint","IMPRINT",EDGE,{"derivedFrom":sQuery(id+"F38.wireOp",EDGE,"E127")}),1.0]])]});
            extrude(context, id + "F40", {"entities" : qUnion([Q0, Q1]), "operationType" : NewBodyOperationType.ADD, "oppositeDirection" : true, "depth" : 12.7 * mm});
        }
        {
            var Q0;
            {var subQ0=sQuery(id+"F38.wireOp",EDGE,"E130.left");Q0=makeQuery(id+"F40.boolean.opBoolean","MERGE",FACE,{"derivedFrom":[makeQuery(id+"F39.opExtrude","SWEPT_FACE",FACE,{"disambiguationData":[OSD([subQ0])]}),makeQuery(id+"F40.opExtrude","SWEPT_FACE",FACE,{"disambiguationData":[OSD([subQ0])]})]});}
            var sketch = newSketch(context, id + "F41", { "sketchPlane" : qUnion([Q0])});
            skLineSegment(sketch, "E134", {"start": v(-19.05, -158.75) * mm, "end": v(12.7, -158.75) * mm, "construction": true});
            skCircle(sketch, "E135", {"center": v(6.35, -158.75) * mm, "radius": 2.54 * mm});
            skSolve(sketch);
        }
        {
            var Q0;
            Q0=makeQuery(id+"F41.imprint","IMPRINT",FACE,{"disambiguationData":[TD([[makeQuery(id+"F41.imprint","IMPRINT",EDGE,{"derivedFrom":sQuery(id+"F41.wireOp",EDGE,"E135")}),1.0]])]});
            extrude(context, id + "F42", {"entities" : qUnion([Q0]), "operationType" : NewBodyOperationType.REMOVE, "endBound" : BoundingType.UP_TO_NEXT, "oppositeDirection" : true, "depth" : 25.4 * mm, "hasSecondDirection" : true, "secondDirectionBound" : SecondDirectionBoundingType.THROUGH_ALL, "secondDirectionOppositeDirection" : false, "secondDirectionDepth" : 25.4 * mm});
        }
        {
            var Q0;
            Q0=qCreatedBy(makeId("Front.planeOp"),FACE);
            var sketch = newSketch(context, id + "F43", { "sketchPlane" : qUnion([Q0])});
            skPoint(sketch, "E136", {"position": v(0, 406.4) * mm});
            skCircle(sketch, "E137", {"center": v(0, 406.4) * mm, "radius": 127 * mm});
            skLineSegment(sketch, "E138", {"start": v(0, 279.4) * mm, "end": v(0, 533.4) * mm, "construction": true});
            skLineSegment(sketch, "E139", {"start": v(0, 406.4) * mm, "end": v(-84.98, 500.78) * mm, "construction": true});
            skLineSegment(sketch, "E140.MirrorCS", {"start": v(0, 406.4) * mm, "end": v(84.98, 500.78) * mm, "construction": true});
            skLineSegment(sketch, "E141", {"start": v(-127, 406.4) * mm, "end": v(127, 406.4) * mm, "construction": true});
            skLineSegment(sketch, "E142.MirrorCS", {"start": v(0, 406.4) * mm, "end": v(-84.98, 312.02) * mm, "construction": true});
            skLineSegment(sketch, "E143.MirrorCS", {"start": v(0, 406.4) * mm, "end": v(84.98, 312.02) * mm, "construction": true});
            skCircle(sketch, "E144", {"center": v(0, 406.4) * mm, "radius": 95.25 * mm});
            skLineSegment(sketch, "E145", {"start": v(-84.98, 500.78) * mm, "end": v(-63.73, 477.18) * mm});
            skLineSegment(sketch, "E146", {"start": v(63.73, 477.18) * mm, "end": v(84.98, 500.78) * mm});
            skLineSegment(sketch, "E147", {"start": v(63.73, 335.62) * mm, "end": v(84.98, 312.02) * mm});
            skLineSegment(sketch, "E148", {"start": v(-63.73, 335.62) * mm, "end": v(-84.98, 312.02) * mm});
            skLineSegment(sketch, "E149.bottom", {"start": v(-19.05, 425.45) * mm, "end": v(19.05, 425.45) * mm});
            skLineSegment(sketch, "E149.top", {"start": v(-19.05, 387.35) * mm, "end": v(19.05, 387.35) * mm});
            skLineSegment(sketch, "E149.left", {"start": v(-19.05, 425.45) * mm, "end": v(-19.05, 387.35) * mm});
            skLineSegment(sketch, "E149.right", {"start": v(19.05, 425.45) * mm, "end": v(19.05, 387.35) * mm});
            skLineSegment(sketch, "E150", {"start": v(-19.05, 425.45) * mm, "end": v(0, 406.4) * mm, "construction": true});
            skLineSegment(sketch, "E151", {"start": v(0, 406.4) * mm, "end": v(19.05, 425.45) * mm, "construction": true});
            skLineSegment(sketch, "E152", {"start": v(0, 406.4) * mm, "end": v(19.05, 387.35) * mm, "construction": true});
            skLineSegment(sketch, "E153", {"start": v(0, 406.4) * mm, "end": v(-19.05, 387.35) * mm, "construction": true});
            skCircle(sketch, "E154", {"center": v(-15.88, 422.28) * mm, "radius": 4.5 * mm});
            skPoint(sketch, "E154.first.point", {"position": v(-12.7, 425.45) * mm});
            skPoint(sketch, "E154.second.point", {"position": v(-19.05, 419.1) * mm});
            skCircle(sketch, "E155.MirrorC", {"center": v(15.88, 422.28) * mm, "radius": 4.5 * mm});
            skCircle(sketch, "E156.MirrorC", {"center": v(15.88, 390.52) * mm, "radius": 4.5 * mm});
            skCircle(sketch, "E157.MirrorC", {"center": v(-15.88, 390.52) * mm, "radius": 4.5 * mm});
            skCircle(sketch, "E158", {"center": v(0, 441.96) * mm, "radius": 3.81 * mm});
            skCircle(sketch, "E159.MirrorC", {"center": v(0, 370.84) * mm, "radius": 3.81 * mm});
            skCircle(sketch, "E160", {"center": v(-35.56, 406.4) * mm, "radius": 3.81 * mm});
            skCircle(sketch, "E161.MirrorC", {"center": v(35.56, 406.4) * mm, "radius": 3.81 * mm});
            skSolve(sketch);
        }
        {
            var Q0;
            {var subQ0=sQuery(id+"F43.wireOp",EDGE,"E144");var subQ1=makeQuery(id+"F43.imprint","INTERSECT",VERTEX,{"derivedFrom":[subQ0,sQuery(id+"F43.wireOp",EDGE,"E145")]});Q0=makeQuery(id+"F43.imprint","IMPRINT",FACE,{"disambiguationData":[TD([[makeQuery(id+"F43.imprint","IMPRINT",EDGE,{"disambiguationData":[TD([[subQ1,1.0]])],"derivedFrom":subQ0}),1.0]])]});}
            var Q1;
            {var subQ0=sQuery(id+"F43.wireOp",EDGE,"E145");Q1=makeQuery(id+"F43.imprint","IMPRINT",FACE,{"disambiguationData":[TD([[makeQuery(id+"F43.imprint","IMPRINT",EDGE,{"derivedFrom":subQ0}),-1.0]])]});}
            var Q2;
            {var subQ0=sQuery(id+"F43.wireOp",EDGE,"E146");Q2=makeQuery(id+"F43.imprint","IMPRINT",FACE,{"disambiguationData":[TD([[makeQuery(id+"F43.imprint","IMPRINT",EDGE,{"derivedFrom":subQ0}),-1.0]])]});}
            extrude(context, id + "F44", {"entities" : qUnion([Q0, Q1, Q2]), "depth" : 19.05 * mm});
        }
        {
            var Q0;
            Q0=makeQuery(id+"F44.opExtrude","SWEPT_EDGE",EDGE,{"disambiguationData":[OSD([sQuery(id+"F43.wireOp",EDGE,"E137"),sQuery(id+"F43.wireOp",EDGE,"E145")])]});
            var Q1;
            Q1=makeQuery(id+"F44.opExtrude","SWEPT_EDGE",EDGE,{"disambiguationData":[OSD([sQuery(id+"F43.wireOp",EDGE,"E137"),sQuery(id+"F43.wireOp",EDGE,"E146")])]});
            var Q2;
            Q2=makeQuery(id+"F44.opExtrude","SWEPT_EDGE",EDGE,{"disambiguationData":[OSD([sQuery(id+"F43.wireOp",EDGE,"E137"),sQuery(id+"F43.wireOp",EDGE,"E147")])]});
            var Q3;
            Q3=makeQuery(id+"F44.opExtrude","SWEPT_EDGE",EDGE,{"disambiguationData":[OSD([sQuery(id+"F43.wireOp",EDGE,"E137"),sQuery(id+"F43.wireOp",EDGE,"E148")])]});
            fillet(context, id + "F45", {"entities" : qUnion([Q0, Q1, Q2, Q3]), "radius" : 5.08 * mm, "tangentPropagation" : true, "allowEdgeOverflow" : false});
        }
        {
            var Q0;
            Q0=makeQuery(id+"F44.opExtrude","SWEPT_EDGE",EDGE,{"disambiguationData":[OSD([sQuery(id+"F43.wireOp",EDGE,"E144"),sQuery(id+"F43.wireOp",EDGE,"E145")])]});
            var Q1;
            Q1=makeQuery(id+"F44.opExtrude","SWEPT_EDGE",EDGE,{"disambiguationData":[OSD([sQuery(id+"F43.wireOp",EDGE,"E144"),sQuery(id+"F43.wireOp",EDGE,"E146")])]});
            var Q2;
            Q2=makeQuery(id+"F44.opExtrude","SWEPT_EDGE",EDGE,{"disambiguationData":[OSD([sQuery(id+"F43.wireOp",EDGE,"E144"),sQuery(id+"F43.wireOp",EDGE,"E148")])]});
            var Q3;
            Q3=makeQuery(id+"F44.opExtrude","SWEPT_EDGE",EDGE,{"disambiguationData":[OSD([sQuery(id+"F43.wireOp",EDGE,"E144"),sQuery(id+"F43.wireOp",EDGE,"E147")])]});
            fillet(context, id + "F46", {"entities" : qUnion([Q0, Q1, Q2, Q3]), "radius" : 7.62 * mm, "tangentPropagation" : true, "allowEdgeOverflow" : false});
        }
        {
            var Q0;
            Q0=qCreatedBy(makeId("Front.planeOp"),FACE);
            cPlane(context, id + "F47", {"entities" : qUnion([Q0]), "cplaneType" : CPlaneType.OFFSET, "offset" : 152.4 * mm, "oppositeDirection" : true, "width" : 152.4 * mm, "height" : 152.4 * mm});
        }
        {
            var Q0;
            Q0=qCreatedBy(id+"F47.planeOp",FACE);
            var sketch = newSketch(context, id + "F48", { "sketchPlane" : qUnion([Q0])});
            skLineSegment(sketch, "E162", {"start": v(151.1, 406.4) * mm, "end": v(-145.38, 406.4) * mm, "construction": true});
            skPoint(sketch, "E162.endSnap0", {"position": v(-127, 406.4) * mm});
            skLineSegment(sketch, "E163", {"start": v(0, 543.51) * mm, "end": v(0, 270.41) * mm, "construction": true});
            skArc(sketch, "E164.converted", {"start": v(-83.32, 502.25) * mm, "mid": v(-115.57, 459.07) * mm, "end": v(-127, 406.4) * mm});
            skCircle(sketch, "E165", {"center": v(0, 406.4) * mm, "radius": 127 * mm, "construction": true});
            skLineSegment(sketch, "E166", {"start": v(0, 406.4) * mm, "end": v(123.26, 513.55) * mm, "construction": true});
            skLineSegment(sketch, "E167", {"start": v(0, 406.4) * mm, "end": v(-123.4, 299.13) * mm, "construction": true});
            skLineSegment(sketch, "E168", {"start": v(0, 406.4) * mm, "end": v(-94.9, 515.57) * mm, "construction": true});
            skLineSegment(sketch, "E169", {"start": v(0, 406.4) * mm, "end": v(104.16, 286.57) * mm, "construction": true});
            skArc(sketch, "E170.trimOffspring", {"start": v(95.85, 489.72) * mm, "mid": v(52.67, 521.97) * mm, "end": v(0, 533.4) * mm});
            skArc(sketch, "E171.trimOffspring", {"start": v(83.32, 310.55) * mm, "mid": v(115.57, 353.73) * mm, "end": v(127, 406.4) * mm});
            skArc(sketch, "E172.trimOffspring", {"start": v(-95.85, 323.08) * mm, "mid": v(-52.67, 290.83) * mm, "end": v(0, 279.4) * mm});
            skLineSegment(sketch, "E173", {"start": v(-83.32, 502.25) * mm, "end": v(-66.66, 483.08) * mm});
            skLineSegment(sketch, "E174", {"start": v(0, 533.4) * mm, "end": v(0, 508) * mm});
            skLineSegment(sketch, "E175", {"start": v(95.85, 489.72) * mm, "end": v(76.68, 473.06) * mm});
            skLineSegment(sketch, "E176", {"start": v(127, 406.4) * mm, "end": v(101.6, 406.4) * mm});
            skLineSegment(sketch, "E177", {"start": v(83.32, 310.55) * mm, "end": v(66.66, 329.72) * mm});
            skLineSegment(sketch, "E178", {"start": v(0, 279.4) * mm, "end": v(0, 304.8) * mm});
            skLineSegment(sketch, "E179", {"start": v(-95.85, 323.08) * mm, "end": v(-76.68, 339.74) * mm});
            skLineSegment(sketch, "E180", {"start": v(-127, 406.4) * mm, "end": v(-101.6, 406.4) * mm});
            skArc(sketch, "E181", {"start": v(-66.66, 483.08) * mm, "mid": v(-35.58, 501.57) * mm, "end": v(0, 508) * mm});
            skArc(sketch, "E182", {"start": v(76.68, 473.06) * mm, "mid": v(95.17, 441.98) * mm, "end": v(101.6, 406.4) * mm});
            skArc(sketch, "E183", {"start": v(66.66, 329.72) * mm, "mid": v(35.58, 311.23) * mm, "end": v(0, 304.8) * mm});
            skArc(sketch, "E184", {"start": v(-76.68, 339.74) * mm, "mid": v(-95.17, 370.82) * mm, "end": v(-101.6, 406.4) * mm});
            skLineSegment(sketch, "E185", {"start": v(0, 406.4) * mm, "end": v(1.24, 441.96) * mm, "construction": true});
            skLineSegment(sketch, "E186", {"start": v(0, 406.4) * mm, "end": v(35.56, 405.16) * mm, "construction": true});
            skLineSegment(sketch, "E187", {"start": v(0, 406.4) * mm, "end": v(-1.24, 370.84) * mm, "construction": true});
            skLineSegment(sketch, "E188", {"start": v(0, 406.4) * mm, "end": v(-35.56, 407.64) * mm, "construction": true});
            skLineSegment(sketch, "E189", {"start": v(-18.37, 426.1) * mm, "end": v(-19.7, 388.03) * mm});
            skLineSegment(sketch, "E190.MirrorCS", {"start": v(19.7, 424.77) * mm, "end": v(18.37, 386.7) * mm});
            skLineSegment(sketch, "E191", {"start": v(-18.37, 426.1) * mm, "end": v(19.7, 424.77) * mm});
            skLineSegment(sketch, "E192", {"start": v(18.37, 386.7) * mm, "end": v(-19.7, 388.03) * mm});
            skCircle(sketch, "E193", {"center": v(1.24, 441.96) * mm, "radius": 3.81 * mm});
            skCircle(sketch, "E194", {"center": v(35.56, 405.16) * mm, "radius": 3.81 * mm});
            skCircle(sketch, "E195", {"center": v(-1.24, 370.84) * mm, "radius": 3.81 * mm});
            skCircle(sketch, "E196", {"center": v(-35.56, 407.64) * mm, "radius": 3.81 * mm});
            skCircle(sketch, "E197", {"center": v(-15.31, 422.82) * mm, "radius": 4.5 * mm});
            skPoint(sketch, "E197.first.point", {"position": v(-12.03, 425.88) * mm});
            skPoint(sketch, "E197.third.point", {"position": v(-18.6, 419.76) * mm});
            skLineSegment(sketch, "E198", {"start": v(-18.37, 426.1) * mm, "end": v(18.37, 386.7) * mm, "construction": true});
            skLineSegment(sketch, "E199", {"start": v(19.7, 424.77) * mm, "end": v(-19.7, 388.03) * mm, "construction": true});
            skCircle(sketch, "E200.MirrorC", {"center": v(16.42, 421.71) * mm, "radius": 4.5 * mm});
            skCircle(sketch, "E201.MirrorC", {"center": v(-16.42, 391.09) * mm, "radius": 4.5 * mm});
            skCircle(sketch, "E202.MirrorC", {"center": v(15.31, 389.98) * mm, "radius": 4.5 * mm});
            skSolve(sketch);
        }
        {
            var Q0;
            Q0=makeQuery(id+"F48.imprint","IMPRINT",FACE,{"disambiguationData":[TD([[makeQuery(id+"F48.imprint","IMPRINT",EDGE,{"derivedFrom":sQuery(id+"F48.wireOp",EDGE,"E164.converted")}),1.0]])]});
            extrude(context, id + "F49", {"entities" : qUnion([Q0]), "depth" : 12.7 * mm});
        }
        {
            var Q0;
            Q0=makeQuery(id+"F49.opExtrude","SWEPT_EDGE",EDGE,{"disambiguationData":[OSD([sQuery(id+"F48.wireOp",EDGE,"E170.trimOffspring"),sQuery(id+"F48.wireOp",EDGE,"E175")])]});
            var Q1;
            Q1=makeQuery(id+"F49.opExtrude","SWEPT_EDGE",EDGE,{"disambiguationData":[OSD([sQuery(id+"F48.wireOp",EDGE,"E171.trimOffspring"),sQuery(id+"F48.wireOp",EDGE,"E176")])]});
            var Q2;
            Q2=makeQuery(id+"F49.opExtrude","SWEPT_EDGE",EDGE,{"disambiguationData":[OSD([sQuery(id+"F48.wireOp",EDGE,"E171.trimOffspring"),sQuery(id+"F48.wireOp",EDGE,"E177")])]});
            var Q3;
            Q3=makeQuery(id+"F49.opExtrude","SWEPT_EDGE",EDGE,{"disambiguationData":[OSD([sQuery(id+"F48.wireOp",EDGE,"E172.trimOffspring"),sQuery(id+"F48.wireOp",EDGE,"E178")])]});
            var Q4;
            Q4=makeQuery(id+"F49.opExtrude","SWEPT_EDGE",EDGE,{"disambiguationData":[OSD([sQuery(id+"F48.wireOp",EDGE,"E172.trimOffspring"),sQuery(id+"F48.wireOp",EDGE,"E179")])]});
            var Q5;
            Q5=makeQuery(id+"F49.opExtrude","SWEPT_EDGE",EDGE,{"disambiguationData":[OSD([sQuery(id+"F48.wireOp",EDGE,"E164.converted"),sQuery(id+"F48.wireOp",EDGE,"E180")])]});
            var Q6;
            Q6=makeQuery(id+"F49.opExtrude","SWEPT_EDGE",EDGE,{"disambiguationData":[OSD([sQuery(id+"F48.wireOp",EDGE,"E164.converted"),sQuery(id+"F48.wireOp",EDGE,"E173")])]});
            var Q7;
            Q7=makeQuery(id+"F49.opExtrude","SWEPT_EDGE",EDGE,{"disambiguationData":[OSD([sQuery(id+"F48.wireOp",EDGE,"E170.trimOffspring"),sQuery(id+"F48.wireOp",EDGE,"E174")])]});
            fillet(context, id + "F50", {"entities" : qUnion([Q0, Q1, Q2, Q3, Q4, Q5, Q6, Q7]), "radius" : 5.08 * mm, "tangentPropagation" : true, "allowEdgeOverflow" : false});
        }
        {
            var Q0;
            Q0=makeQuery(id+"F49.opExtrude","SWEPT_EDGE",EDGE,{"disambiguationData":[OSD([sQuery(id+"F48.wireOp",EDGE,"E174"),sQuery(id+"F48.wireOp",EDGE,"E181")])]});
            var Q1;
            Q1=makeQuery(id+"F49.opExtrude","SWEPT_EDGE",EDGE,{"disambiguationData":[OSD([sQuery(id+"F48.wireOp",EDGE,"E175"),sQuery(id+"F48.wireOp",EDGE,"E182")])]});
            var Q2;
            Q2=makeQuery(id+"F49.opExtrude","SWEPT_EDGE",EDGE,{"disambiguationData":[OSD([sQuery(id+"F48.wireOp",EDGE,"E176"),sQuery(id+"F48.wireOp",EDGE,"E182")])]});
            var Q3;
            Q3=makeQuery(id+"F49.opExtrude","SWEPT_EDGE",EDGE,{"disambiguationData":[OSD([sQuery(id+"F48.wireOp",EDGE,"E177"),sQuery(id+"F48.wireOp",EDGE,"E183")])]});
            var Q4;
            Q4=makeQuery(id+"F49.opExtrude","SWEPT_EDGE",EDGE,{"disambiguationData":[OSD([sQuery(id+"F48.wireOp",EDGE,"E178"),sQuery(id+"F48.wireOp",EDGE,"E183")])]});
            var Q5;
            Q5=makeQuery(id+"F49.opExtrude","SWEPT_EDGE",EDGE,{"disambiguationData":[OSD([sQuery(id+"F48.wireOp",EDGE,"E179"),sQuery(id+"F48.wireOp",EDGE,"E184")])]});
            var Q6;
            Q6=makeQuery(id+"F49.opExtrude","SWEPT_EDGE",EDGE,{"disambiguationData":[OSD([sQuery(id+"F48.wireOp",EDGE,"E180"),sQuery(id+"F48.wireOp",EDGE,"E184")])]});
            var Q7;
            Q7=makeQuery(id+"F49.opExtrude","SWEPT_EDGE",EDGE,{"disambiguationData":[OSD([sQuery(id+"F48.wireOp",EDGE,"E173"),sQuery(id+"F48.wireOp",EDGE,"E181")])]});
            fillet(context, id + "F51", {"entities" : qUnion([Q0, Q1, Q2, Q3, Q4, Q5, Q6, Q7]), "radius" : 7.62 * mm, "tangentPropagation" : true, "allowEdgeOverflow" : false});
        }
        {
            var Q0;
            Q0=qCreatedBy(id+"F47.planeOp",FACE);
            var sketch = newSketch(context, id + "F52", { "sketchPlane" : qUnion([Q0])});
            skCircle(sketch, "E203", {"center": v(355.6, 406.4) * mm, "radius": 146.05 * mm, "construction": true});
            skArc(sketch, "E204.0", {"start": v(-87.24, 498.7) * mm, "mid": v(-115.57, 459.07) * mm, "end": v(-126.89, 411.7) * mm, "construction": true});
            skArc(sketch, "E205", {"start": v(335.75, 518.96) * mm, "mid": v(256.61, 349.25) * mm, "end": v(443.16, 332.93) * mm});
            skLineSegment(sketch, "E206", {"start": v(355.6, 406.4) * mm, "end": v(355.6, 552.45) * mm, "construction": true});
            skLineSegment(sketch, "E207", {"start": v(375.45, 518.96) * mm, "end": v(380.96, 550.23) * mm});
            skLineSegment(sketch, "E208.MirrorCS", {"start": v(335.75, 518.96) * mm, "end": v(330.24, 550.23) * mm});
            skArc(sketch, "E209", {"start": v(330.24, 550.23) * mm, "mid": v(355.6, 552.45) * mm, "end": v(380.96, 550.23) * mm});
            skCircle(sketch, "E210", {"center": v(660.4, 406.4) * mm, "radius": 152.4 * mm});
            skLineSegment(sketch, "E211", {"start": v(355.6, 406.4) * mm, "end": v(482.08, 333.38) * mm, "construction": true});
            skLineSegment(sketch, "E212", {"start": v(463, 367.3) * mm, "end": v(492.84, 356.45) * mm});
            skLineSegment(sketch, "E213.MirrorCS", {"start": v(443.16, 332.93) * mm, "end": v(467.48, 312.52) * mm});
            skArc(sketch, "E214", {"start": v(492.84, 356.45) * mm, "mid": v(482.08, 333.38) * mm, "end": v(467.48, 312.52) * mm});
            skArc(sketch, "E215.trimOffspring", {"start": v(463, 367.3) * mm, "mid": v(454.59, 463.55) * mm, "end": v(375.45, 518.96) * mm});
            skSolve(sketch);
        }
        {
            var Q0;
            Q0=makeQuery(id+"F52.imprint","IMPRINT",FACE,{"disambiguationData":[TD([[makeQuery(id+"F52.imprint","IMPRINT",EDGE,{"derivedFrom":sQuery(id+"F52.wireOp",EDGE,"E205")}),1.0]])]});
            extrude(context, id + "F53", {"entities" : qUnion([Q0]), "depth" : 12.7 * mm});
        }
        {
            var Q0;
            Q0=makeQuery(id+"F52.imprint","IMPRINT",FACE,{"disambiguationData":[TD([[makeQuery(id+"F52.imprint","IMPRINT",EDGE,{"derivedFrom":sQuery(id+"F52.wireOp",EDGE,"E210")}),1.0]])]});
            extrude(context, id + "F54", {"entities" : qUnion([Q0]), "depth" : 12.7 * mm});
        }
        {
            var Q0;
            Q0=qCreatedBy(id+"F47.planeOp",FACE);
            var sketch = newSketch(context, id + "F55", { "sketchPlane" : qUnion([Q0])});
            skCircle(sketch, "E216", {"center": v(1016, 406.4) * mm, "radius": 127 * mm});
            skLineSegment(sketch, "E217", {"start": v(1016, 406.4) * mm, "end": v(889, 406.4) * mm, "construction": true});
            skLineSegment(sketch, "E218.bottom", {"start": v(895.35, 406.4) * mm, "end": v(971.55, 406.4) * mm});
            skLineSegment(sketch, "E218.top", {"start": v(895.35, 393.7) * mm, "end": v(971.55, 393.7) * mm});
            skLineSegment(sketch, "E218.left", {"start": v(895.35, 406.4) * mm, "end": v(895.35, 393.7) * mm});
            skLineSegment(sketch, "E218.right", {"start": v(971.55, 406.4) * mm, "end": v(971.55, 393.7) * mm});
            skCircle(sketch, "E219.0", {"center": v(660.4, 406.4) * mm, "radius": 152.4 * mm, "construction": true});
            skLineSegment(sketch, "E220", {"start": v(1016, 279.4) * mm, "end": v(1016, 533.4) * mm, "construction": true});
            skLineSegment(sketch, "E221.bottom", {"start": v(1060.45, 406.4) * mm, "end": v(1136.65, 406.4) * mm});
            skLineSegment(sketch, "E221.top", {"start": v(1060.45, 419.1) * mm, "end": v(1136.65, 419.1) * mm});
            skLineSegment(sketch, "E221.left", {"start": v(1060.45, 406.4) * mm, "end": v(1060.45, 419.1) * mm});
            skLineSegment(sketch, "E221.right", {"start": v(1136.65, 406.4) * mm, "end": v(1136.65, 419.1) * mm});
            skLineSegment(sketch, "E222", {"start": v(1016, 406.4) * mm, "end": v(1143, 406.4) * mm, "construction": true});
            skSolve(sketch);
        }
        {
            var Q0;
            Q0=makeQuery(id+"F55.imprint","IMPRINT",FACE,{"disambiguationData":[TD([[makeQuery(id+"F55.imprint","IMPRINT",EDGE,{"derivedFrom":sQuery(id+"F55.wireOp",EDGE,"E216")}),1.0]])]});
            extrude(context, id + "F56", {"entities" : qUnion([Q0]), "depth" : 12.7 * mm});
        }
        {
            var Q0;
            Q0=makeQuery(id+"F55.imprint","IMPRINT",FACE,{"disambiguationData":[TD([[makeQuery(id+"F55.imprint","IMPRINT",EDGE,{"derivedFrom":sQuery(id+"F55.wireOp",EDGE,"E218.bottom")}),-1.0]])]});
            var Q1;
            Q1=makeQuery(id+"F55.imprint","IMPRINT",FACE,{"disambiguationData":[TD([[makeQuery(id+"F55.imprint","IMPRINT",EDGE,{"derivedFrom":sQuery(id+"F55.wireOp",EDGE,"E221.bottom")}),1.0]])]});
            extrude(context, id + "F57", {"entities" : qUnion([Q0, Q1]), "operationType" : NewBodyOperationType.ADD, "depth" : 25.4 * mm});
        }
        {
            var Q0;
            Q0=qCreatedBy(id+"F15.planeOp",FACE);
            var sketch = newSketch(context, id + "F58", { "sketchPlane" : qUnion([Q0])});
            skLineSegment(sketch, "E223.0", {"start": v(812.8, 152.4) * mm, "end": v(508, 152.4) * mm, "construction": true});
            skLineSegment(sketch, "E224.0", {"start": v(812.8, 139.7) * mm, "end": v(508, 139.7) * mm, "construction": true});
            skLineSegment(sketch, "E225", {"start": v(660.4, 152.4) * mm, "end": v(660.4, 139.7) * mm, "construction": true});
            skCircle(sketch, "E226", {"center": v(660.4, 146.05) * mm, "radius": 3.2 * mm});
            skSolve(sketch);
        }
        {
            var Q0;
            Q0 = qSketchRegion(id + "F58", true);
            extrude(context, id + "F59", {"entities" : qUnion([Q0]), "operationType" : NewBodyOperationType.REMOVE, "endBound" : BoundingType.THROUGH_ALL, "depth" : 25.4 * mm});
        }
    });
